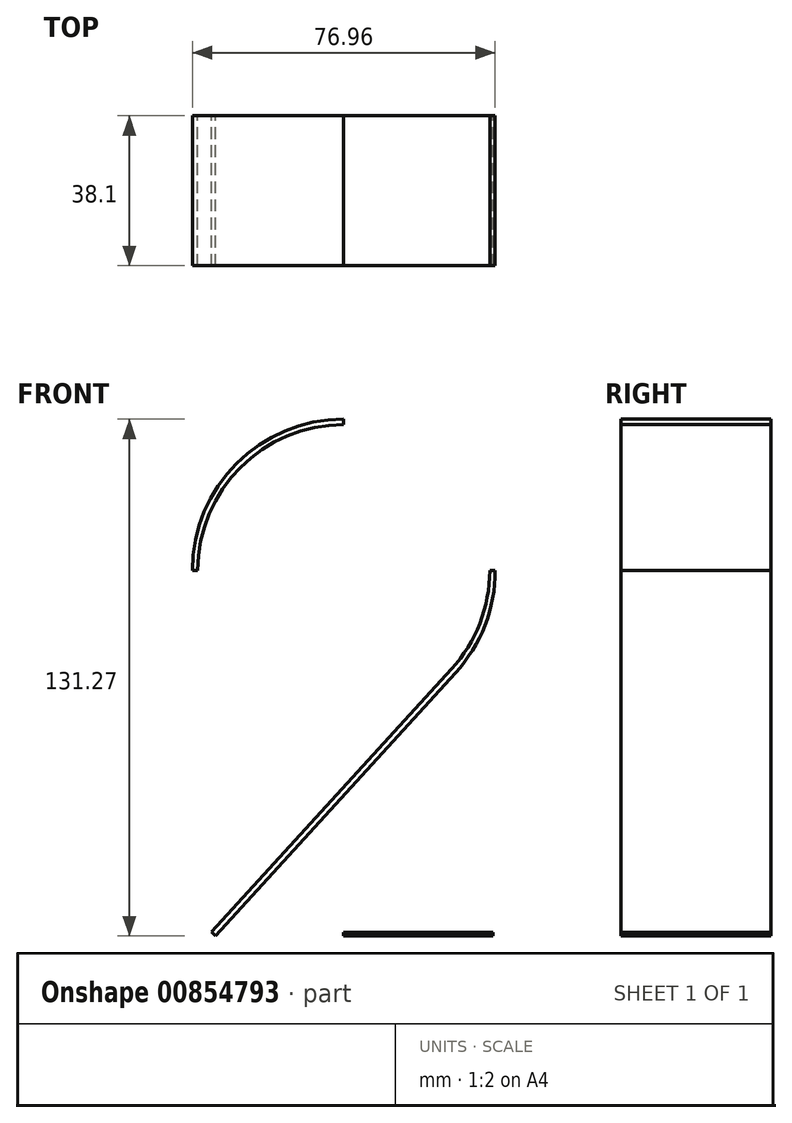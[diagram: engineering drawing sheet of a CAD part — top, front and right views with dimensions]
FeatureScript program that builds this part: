
annotation { "Feature Type Name" : "Feature", "Feature Type Description" : "" }
export const myFeature = defineFeature(function(context is Context, id is Id, definition is map)
    precondition{}
    {
        {
            var Q0;
            Q0=qCreatedBy(makeId("Front.planeOp"),FACE);
            var sketch = newSketch(context, id + "F0", { "sketchPlane" : qUnion([Q0])});
            skArc(sketch, "E0", {"start": v(28.42, -25.94) * mm, "mid": v(35.88, -13.91) * mm, "end": v(38.48, 0) * mm});
            skLineSegment(sketch, "E1", {"start": v(28.42, -25.94) * mm, "end": v(-32.6, -92.79) * mm});
            skLineSegment(sketch, "E2", {"start": v(0, -92.79) * mm, "end": v(37.93, -92.79) * mm});
            skLineSegment(sketch, "E3", {"start": v(-55.8, 0) * mm, "end": v(59, 0) * mm, "construction": true});
            skLineSegment(sketch, "E4", {"start": v(0, 61.16) * mm, "end": v(0, -97.48) * mm, "construction": true});
            skArc(sketch, "E5.trimOffspring", {"start": v(0, 38.48) * mm, "mid": v(-27.2, 27.2) * mm, "end": v(-38.48, 0) * mm});
            skArc(sketch, "E6", {"start": v(27.4, -25) * mm, "mid": v(34.58, -13.4) * mm, "end": v(37.09, 0) * mm});
            skArc(sketch, "E7.trimOffspring", {"start": v(0, 37.09) * mm, "mid": v(-26.23, 26.23) * mm, "end": v(-37.09, 0) * mm});
            skLineSegment(sketch, "E8", {"start": v(0, 0) * mm, "end": v(28.42, -25.94) * mm, "construction": true});
            skLineSegment(sketch, "E9", {"start": v(27.4, -25) * mm, "end": v(-33.62, -91.85) * mm});
            skLineSegment(sketch, "E10", {"start": v(-38.48, 0) * mm, "end": v(-37.09, 0) * mm});
            skLineSegment(sketch, "E11", {"start": v(0, 38.48) * mm, "end": v(0, 37.09) * mm});
            skLineSegment(sketch, "E12", {"start": v(37.09, 0) * mm, "end": v(38.48, 0) * mm});
            skLineSegment(sketch, "E13", {"start": v(-32.6, -92.79) * mm, "end": v(-33.62, -91.85) * mm});
            skLineSegment(sketch, "E14", {"start": v(0, -92.79) * mm, "end": v(0, -91.89) * mm});
            skLineSegment(sketch, "E15", {"start": v(0, -91.89) * mm, "end": v(37.93, -91.89) * mm});
            skLineSegment(sketch, "E16", {"start": v(37.93, -91.89) * mm, "end": v(37.93, -92.79) * mm});
            skSolve(sketch);
        }
        {
            var Q0;
            Q0 = qSketchRegion(id + "F0", true);
            extrude(context, id + "F1", {"entities" : qUnion([Q0]), "depth" : 38.1 * mm, "offsetDistance" : 25.4 * mm});
        }
    });
